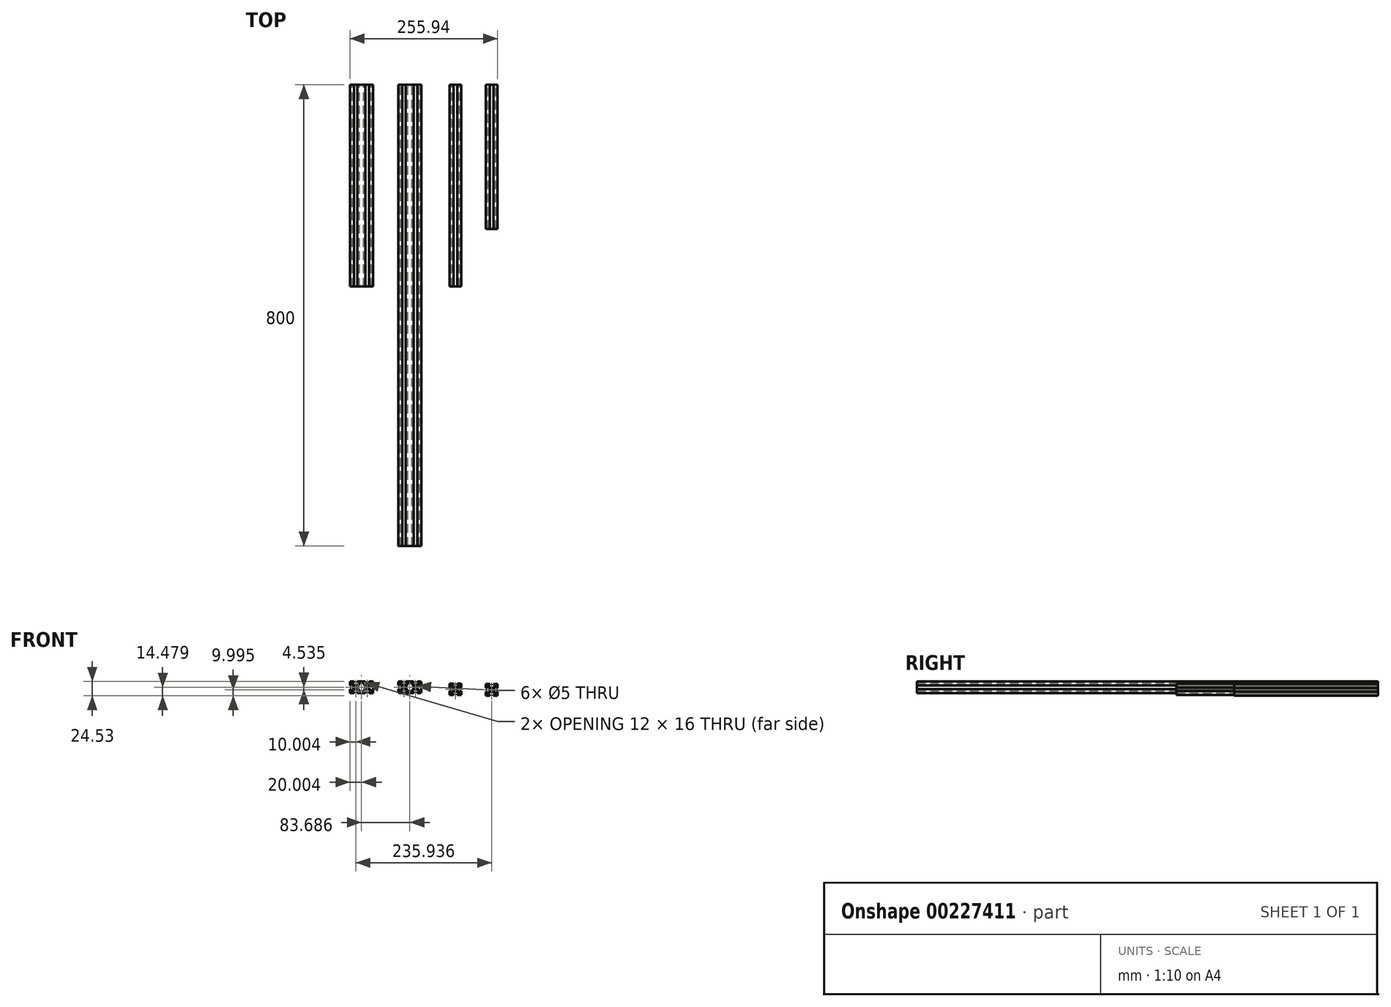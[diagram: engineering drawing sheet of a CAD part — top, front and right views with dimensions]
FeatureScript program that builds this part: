
annotation { "Feature Type Name" : "Feature", "Feature Type Description" : "" }
export const myFeature = defineFeature(function(context is Context, id is Id, definition is map)
    precondition{}
    {
        {
            var Q0;
            Q0=qCreatedBy(makeId("Front.planeOp"),FACE);
            var sketch = newSketch(context, id + "F0", { "sketchPlane" : qUnion([Q0])});
            skLineSegment(sketch, "E0.bottom", {"start": v(-20, 10) * mm, "end": v(-13, 10) * mm});
            skLineSegment(sketch, "E0.top", {"start": v(-20, -10) * mm, "end": v(-13, -10) * mm});
            skLineSegment(sketch, "E0.left", {"start": v(-20, 10) * mm, "end": v(-20, 3) * mm});
            skPoint(sketch, "E1.endSnap0", {"position": v(0, -10) * mm});
            skLineSegment(sketch, "E2", {"start": v(-26.6, 0) * mm, "end": v(32.73, 0) * mm, "construction": true});
            skCircle(sketch, "E3", {"center": v(10, 0) * mm, "radius": 2.5 * mm});
            skCircle(sketch, "E4", {"center": v(-10, 0) * mm, "radius": 2.5 * mm});
            skLineSegment(sketch, "E5", {"start": v(4.5, 8) * mm, "end": v(7, 8) * mm});
            skLineSegment(sketch, "E6", {"start": v(15.5, 8) * mm, "end": v(15.5, 6.5) * mm});
            skLineSegment(sketch, "E7", {"start": v(15.5, 6.5) * mm, "end": v(13, 4) * mm});
            skLineSegment(sketch, "E8", {"start": v(13, 4) * mm, "end": v(7, 4) * mm});
            skLineSegment(sketch, "E9", {"start": v(7, 4) * mm, "end": v(4.5, 6.5) * mm});
            skLineSegment(sketch, "E10", {"start": v(4.5, 6.5) * mm, "end": v(4.5, 8) * mm});
            skLineSegment(sketch, "E11", {"start": v(0, 29.93) * mm, "end": v(0, -23.02) * mm, "construction": true});
            skLineSegment(sketch, "E12", {"start": v(7, 8) * mm, "end": v(7, 10) * mm});
            skLineSegment(sketch, "E13", {"start": v(13, 8) * mm, "end": v(13, 10) * mm});
            skLineSegment(sketch, "E14.trimOffspring", {"start": v(13, 8) * mm, "end": v(15.5, 8) * mm});
            skLineSegment(sketch, "E15.trimOffspring", {"start": v(13, 10) * mm, "end": v(20, 10) * mm});
            skLineSegment(sketch, "E16.1.3", {"start": v(6, -3) * mm, "end": v(3.5, -5.5) * mm});
            skLineSegment(sketch, "E16.1.4", {"start": v(6, 3) * mm, "end": v(6, -3) * mm});
            skLineSegment(sketch, "E16.1.5", {"start": v(3.5, 5.5) * mm, "end": v(6, 3) * mm});
            skLineSegment(sketch, "E16.2.0", {"start": v(13, -8) * mm, "end": v(13, -10) * mm});
            skLineSegment(sketch, "E16.2.1", {"start": v(15.5, -8) * mm, "end": v(13, -8) * mm});
            skLineSegment(sketch, "E16.2.2", {"start": v(15.5, -6.5) * mm, "end": v(15.5, -8) * mm});
            skLineSegment(sketch, "E16.2.3", {"start": v(13, -4) * mm, "end": v(15.5, -6.5) * mm});
            skLineSegment(sketch, "E16.2.4", {"start": v(7, -4) * mm, "end": v(13, -4) * mm});
            skLineSegment(sketch, "E16.2.5", {"start": v(4.5, -6.5) * mm, "end": v(7, -4) * mm});
            skLineSegment(sketch, "E16.2.6", {"start": v(7, -8) * mm, "end": v(7, -10) * mm});
            skLineSegment(sketch, "E16.2.7", {"start": v(7, -8) * mm, "end": v(4.5, -8) * mm});
            skLineSegment(sketch, "E16.2.8", {"start": v(4.5, -8) * mm, "end": v(4.5, -6.5) * mm});
            skLineSegment(sketch, "E16.3.0", {"start": v(18, 3) * mm, "end": v(20, 3) * mm});
            skLineSegment(sketch, "E16.3.1", {"start": v(18, 5.5) * mm, "end": v(18, 3) * mm});
            skLineSegment(sketch, "E16.3.2", {"start": v(16.5, 5.5) * mm, "end": v(18, 5.5) * mm});
            skLineSegment(sketch, "E16.3.3", {"start": v(14, 3) * mm, "end": v(16.5, 5.5) * mm});
            skLineSegment(sketch, "E16.3.4", {"start": v(14, -3) * mm, "end": v(14, 3) * mm});
            skLineSegment(sketch, "E16.3.5", {"start": v(16.5, -5.5) * mm, "end": v(14, -3) * mm});
            skLineSegment(sketch, "E16.3.6", {"start": v(18, -3) * mm, "end": v(20, -3) * mm});
            skLineSegment(sketch, "E16.3.7", {"start": v(18, -3) * mm, "end": v(18, -5.5) * mm});
            skLineSegment(sketch, "E16.3.8", {"start": v(18, -5.5) * mm, "end": v(16.5, -5.5) * mm});
            skLineSegment(sketch, "E17.MirrorCS", {"start": v(-4.5, -8) * mm, "end": v(-4.5, -6.5) * mm});
            skLineSegment(sketch, "E18.MirrorCS", {"start": v(-4.5, -6.5) * mm, "end": v(-7, -4) * mm});
            skLineSegment(sketch, "E19.MirrorCS", {"start": v(-7, -4) * mm, "end": v(-13, -4) * mm});
            skLineSegment(sketch, "E20.MirrorCS", {"start": v(-7, -8) * mm, "end": v(-4.5, -8) * mm});
            skLineSegment(sketch, "E21.MirrorCS", {"start": v(-7, -8) * mm, "end": v(-7, -10) * mm});
            skLineSegment(sketch, "E22.MirrorCS", {"start": v(-13, -8) * mm, "end": v(-13, -10) * mm});
            skLineSegment(sketch, "E23.MirrorCS", {"start": v(-15.5, -8) * mm, "end": v(-13, -8) * mm});
            skLineSegment(sketch, "E24.MirrorCS", {"start": v(-15.5, -6.5) * mm, "end": v(-15.5, -8) * mm});
            skLineSegment(sketch, "E25.MirrorCS", {"start": v(-13, -4) * mm, "end": v(-15.5, -6.5) * mm});
            skLineSegment(sketch, "E26.MirrorCS", {"start": v(-14, -3) * mm, "end": v(-14, 3) * mm});
            skLineSegment(sketch, "E27.MirrorCS", {"start": v(-16.5, -5.5) * mm, "end": v(-14, -3) * mm});
            skLineSegment(sketch, "E28.MirrorCS", {"start": v(-18, -5.5) * mm, "end": v(-16.5, -5.5) * mm});
            skLineSegment(sketch, "E29.MirrorCS", {"start": v(-18, -3) * mm, "end": v(-18, -5.5) * mm});
            skLineSegment(sketch, "E30.MirrorCS", {"start": v(-18, -3) * mm, "end": v(-20, -3) * mm});
            skLineSegment(sketch, "E31.MirrorCS", {"start": v(-18, 3) * mm, "end": v(-20, 3) * mm});
            skLineSegment(sketch, "E32.MirrorCS", {"start": v(-16.5, 5.5) * mm, "end": v(-18, 5.5) * mm});
            skLineSegment(sketch, "E33.MirrorCS", {"start": v(-14, 3) * mm, "end": v(-16.5, 5.5) * mm});
            skLineSegment(sketch, "E34.MirrorCS", {"start": v(-18, 5.5) * mm, "end": v(-18, 3) * mm});
            skLineSegment(sketch, "E35.MirrorCS", {"start": v(-7, 8) * mm, "end": v(-7, 10) * mm});
            skLineSegment(sketch, "E36.MirrorCS", {"start": v(-4.5, 8) * mm, "end": v(-7, 8) * mm});
            skLineSegment(sketch, "E37.MirrorCS", {"start": v(-4.5, 6.5) * mm, "end": v(-4.5, 8) * mm});
            skLineSegment(sketch, "E38.MirrorCS", {"start": v(-7, 4) * mm, "end": v(-4.5, 6.5) * mm});
            skLineSegment(sketch, "E39.MirrorCS", {"start": v(-13, 4) * mm, "end": v(-7, 4) * mm});
            skLineSegment(sketch, "E40.MirrorCS", {"start": v(-15.5, 6.5) * mm, "end": v(-13, 4) * mm});
            skLineSegment(sketch, "E41.MirrorCS", {"start": v(-15.5, 8) * mm, "end": v(-15.5, 6.5) * mm});
            skLineSegment(sketch, "E42.MirrorCS", {"start": v(-13, 8) * mm, "end": v(-15.5, 8) * mm});
            skLineSegment(sketch, "E43.MirrorCS", {"start": v(-13, 8) * mm, "end": v(-13, 10) * mm});
            skLineSegment(sketch, "E44.MirrorCS", {"start": v(-3.5, 5.5) * mm, "end": v(-6, 3) * mm});
            skLineSegment(sketch, "E45.MirrorCS", {"start": v(-6, 3) * mm, "end": v(-6, -3) * mm});
            skLineSegment(sketch, "E46.MirrorCS", {"start": v(-6, -3) * mm, "end": v(-3.5, -5.5) * mm});
            skLineSegment(sketch, "E47", {"start": v(-3.5, 5.5) * mm, "end": v(-3.5, 8) * mm});
            skLineSegment(sketch, "E48", {"start": v(3.5, 5.5) * mm, "end": v(3.5, 8) * mm});
            skLineSegment(sketch, "E49", {"start": v(3.5, 8) * mm, "end": v(-3.5, 8) * mm});
            skLineSegment(sketch, "E50.trimOffspring", {"start": v(-20, -3) * mm, "end": v(-20, -10) * mm});
            skLineSegment(sketch, "E51.trimOffspring", {"start": v(-7, 10) * mm, "end": v(7, 10) * mm});
            skLineSegment(sketch, "E52.trimOffspring", {"start": v(20, -3) * mm, "end": v(20, -10) * mm});
            skLineSegment(sketch, "E53.trimOffspring", {"start": v(13, -10) * mm, "end": v(20, -10) * mm});
            skLineSegment(sketch, "E54.trimOffspring", {"start": v(-7, -10) * mm, "end": v(7, -10) * mm});
            skLineSegment(sketch, "E55.MirrorCS", {"start": v(-3.5, -5.5) * mm, "end": v(-3.5, -8) * mm});
            skLineSegment(sketch, "E56.MirrorCS", {"start": v(3.5, -8) * mm, "end": v(-3.5, -8) * mm});
            skLineSegment(sketch, "E57.MirrorCS", {"start": v(3.5, -5.5) * mm, "end": v(3.5, -8) * mm});
            skLineSegment(sketch, "E58", {"start": v(20, 10) * mm, "end": v(20, 3) * mm});
            skSolve(sketch);
        }
        {
            var Q0;
            Q0 = qSketchRegion(id + "F0", true);
            extrude(context, id + "F1", {"entities" : qUnion([Q0]), "depth" : 800 * mm});
        }
        {
            var Q0;
            Q0=makeQuery(id+"F1.opExtrude","SWEPT_EDGE",EDGE,{"disambiguationData":[OSD([sQuery(id+"F0.wireOp",EDGE,"E15.trimOffspring"),sQuery(id+"F0.wireOp",EDGE,"E58")])]});
            var Q1;
            Q1=makeQuery(id+"F1.opExtrude","SWEPT_EDGE",EDGE,{"disambiguationData":[OSD([sQuery(id+"F0.wireOp",EDGE,"E0.bottom"),sQuery(id+"F0.wireOp",EDGE,"E0.left")])]});
            var Q2;
            Q2=makeQuery(id+"F1.opExtrude","SWEPT_EDGE",EDGE,{"disambiguationData":[OSD([sQuery(id+"F0.wireOp",EDGE,"E0.top"),sQuery(id+"F0.wireOp",EDGE,"E50.trimOffspring")])]});
            var Q3;
            Q3=makeQuery(id+"F1.opExtrude","SWEPT_EDGE",EDGE,{"disambiguationData":[OSD([sQuery(id+"F0.wireOp",EDGE,"E52.trimOffspring"),sQuery(id+"F0.wireOp",EDGE,"E53.trimOffspring")])]});
            fillet(context, id + "F2", {"entities" : qUnion([Q0, Q1, Q2, Q3]), "radius" : 2 * mm, "tangentPropagation" : true, "allowEdgeOverflow" : false});
        }
        {
            var Q0;
            Q0=qCreatedBy(makeId("Front.planeOp"),FACE);
            var sketch = newSketch(context, id + "F3", { "sketchPlane" : qUnion([Q0])});
            skLineSegment(sketch, "E59.bottom", {"start": v(-103.69, 9.95) * mm, "end": v(-96.69, 9.95) * mm});
            skLineSegment(sketch, "E59.top", {"start": v(-103.69, -10.05) * mm, "end": v(-96.69, -10.05) * mm});
            skLineSegment(sketch, "E59.left", {"start": v(-103.69, 9.95) * mm, "end": v(-103.69, 2.95) * mm});
            skPoint(sketch, "E60.endSnap0", {"position": v(-83.69, -10.05) * mm});
            skLineSegment(sketch, "E61", {"start": v(-110.28, -0.05) * mm, "end": v(-50.95, -0.05) * mm, "construction": true});
            skCircle(sketch, "E62", {"center": v(-73.69, -0.05) * mm, "radius": 2.5 * mm});
            skCircle(sketch, "E63", {"center": v(-93.69, -0.05) * mm, "radius": 2.5 * mm});
            skLineSegment(sketch, "E64", {"start": v(-79.19, 7.95) * mm, "end": v(-76.69, 7.95) * mm});
            skLineSegment(sketch, "E65", {"start": v(-68.19, 7.95) * mm, "end": v(-68.19, 6.45) * mm});
            skLineSegment(sketch, "E66", {"start": v(-68.19, 6.45) * mm, "end": v(-70.69, 3.95) * mm});
            skLineSegment(sketch, "E67", {"start": v(-70.69, 3.95) * mm, "end": v(-76.69, 3.95) * mm});
            skLineSegment(sketch, "E68", {"start": v(-76.69, 3.95) * mm, "end": v(-79.19, 6.45) * mm});
            skLineSegment(sketch, "E69", {"start": v(-79.19, 6.45) * mm, "end": v(-79.19, 7.95) * mm});
            skLineSegment(sketch, "E70", {"start": v(-83.69, 29.88) * mm, "end": v(-83.69, -23.07) * mm, "construction": true});
            skLineSegment(sketch, "E71", {"start": v(-76.69, 7.95) * mm, "end": v(-76.69, 9.95) * mm});
            skLineSegment(sketch, "E72", {"start": v(-70.69, 7.95) * mm, "end": v(-70.69, 9.95) * mm});
            skLineSegment(sketch, "E73.trimOffspring", {"start": v(-70.69, 7.95) * mm, "end": v(-68.19, 7.95) * mm});
            skLineSegment(sketch, "E74.trimOffspring", {"start": v(-70.69, 9.95) * mm, "end": v(-63.69, 9.95) * mm});
            skLineSegment(sketch, "E75.1.3", {"start": v(-77.69, -3.05) * mm, "end": v(-80.19, -5.55) * mm});
            skLineSegment(sketch, "E75.1.4", {"start": v(-77.69, 2.95) * mm, "end": v(-77.69, -3.05) * mm});
            skLineSegment(sketch, "E75.1.5", {"start": v(-80.19, 5.45) * mm, "end": v(-77.69, 2.95) * mm});
            skLineSegment(sketch, "E75.2.0", {"start": v(-70.69, -8.05) * mm, "end": v(-70.69, -10.05) * mm});
            skLineSegment(sketch, "E75.2.1", {"start": v(-68.19, -8.05) * mm, "end": v(-70.69, -8.05) * mm});
            skLineSegment(sketch, "E75.2.2", {"start": v(-68.19, -6.55) * mm, "end": v(-68.19, -8.05) * mm});
            skLineSegment(sketch, "E75.2.3", {"start": v(-70.69, -4.05) * mm, "end": v(-68.19, -6.55) * mm});
            skLineSegment(sketch, "E75.2.4", {"start": v(-76.69, -4.05) * mm, "end": v(-70.69, -4.05) * mm});
            skLineSegment(sketch, "E75.2.5", {"start": v(-79.19, -6.55) * mm, "end": v(-76.69, -4.05) * mm});
            skLineSegment(sketch, "E75.2.6", {"start": v(-76.69, -8.05) * mm, "end": v(-76.69, -10.05) * mm});
            skLineSegment(sketch, "E75.2.7", {"start": v(-76.69, -8.05) * mm, "end": v(-79.19, -8.05) * mm});
            skLineSegment(sketch, "E75.2.8", {"start": v(-79.19, -8.05) * mm, "end": v(-79.19, -6.55) * mm});
            skLineSegment(sketch, "E75.3.0", {"start": v(-65.69, 2.95) * mm, "end": v(-63.69, 2.95) * mm});
            skLineSegment(sketch, "E75.3.1", {"start": v(-65.69, 5.45) * mm, "end": v(-65.69, 2.95) * mm});
            skLineSegment(sketch, "E75.3.2", {"start": v(-67.19, 5.45) * mm, "end": v(-65.69, 5.45) * mm});
            skLineSegment(sketch, "E75.3.3", {"start": v(-69.69, 2.95) * mm, "end": v(-67.19, 5.45) * mm});
            skLineSegment(sketch, "E75.3.4", {"start": v(-69.69, -3.05) * mm, "end": v(-69.69, 2.95) * mm});
            skLineSegment(sketch, "E75.3.5", {"start": v(-67.19, -5.55) * mm, "end": v(-69.69, -3.05) * mm});
            skLineSegment(sketch, "E75.3.6", {"start": v(-65.69, -3.05) * mm, "end": v(-63.69, -3.05) * mm});
            skLineSegment(sketch, "E75.3.7", {"start": v(-65.69, -3.05) * mm, "end": v(-65.69, -5.55) * mm});
            skLineSegment(sketch, "E75.3.8", {"start": v(-65.69, -5.55) * mm, "end": v(-67.19, -5.55) * mm});
            skLineSegment(sketch, "E76.MirrorCS", {"start": v(-88.19, -8.05) * mm, "end": v(-88.19, -6.55) * mm});
            skLineSegment(sketch, "E77.MirrorCS", {"start": v(-88.19, -6.55) * mm, "end": v(-90.69, -4.05) * mm});
            skLineSegment(sketch, "E78.MirrorCS", {"start": v(-90.69, -4.05) * mm, "end": v(-96.69, -4.05) * mm});
            skLineSegment(sketch, "E79.MirrorCS", {"start": v(-90.69, -8.05) * mm, "end": v(-88.19, -8.05) * mm});
            skLineSegment(sketch, "E80.MirrorCS", {"start": v(-90.69, -8.05) * mm, "end": v(-90.69, -10.05) * mm});
            skLineSegment(sketch, "E81.MirrorCS", {"start": v(-96.69, -8.05) * mm, "end": v(-96.69, -10.05) * mm});
            skLineSegment(sketch, "E82.MirrorCS", {"start": v(-99.19, -8.05) * mm, "end": v(-96.69, -8.05) * mm});
            skLineSegment(sketch, "E83.MirrorCS", {"start": v(-99.19, -6.55) * mm, "end": v(-99.19, -8.05) * mm});
            skLineSegment(sketch, "E84.MirrorCS", {"start": v(-96.69, -4.05) * mm, "end": v(-99.19, -6.55) * mm});
            skLineSegment(sketch, "E85.MirrorCS", {"start": v(-97.69, -3.05) * mm, "end": v(-97.69, 2.95) * mm});
            skLineSegment(sketch, "E86.MirrorCS", {"start": v(-100.19, -5.55) * mm, "end": v(-97.69, -3.05) * mm});
            skLineSegment(sketch, "E87.MirrorCS", {"start": v(-101.69, -5.55) * mm, "end": v(-100.19, -5.55) * mm});
            skLineSegment(sketch, "E88.MirrorCS", {"start": v(-101.69, -3.05) * mm, "end": v(-101.69, -5.55) * mm});
            skLineSegment(sketch, "E89.MirrorCS", {"start": v(-101.69, -3.05) * mm, "end": v(-103.69, -3.05) * mm});
            skLineSegment(sketch, "E90.MirrorCS", {"start": v(-101.69, 2.95) * mm, "end": v(-103.69, 2.95) * mm});
            skLineSegment(sketch, "E91.MirrorCS", {"start": v(-100.19, 5.45) * mm, "end": v(-101.69, 5.45) * mm});
            skLineSegment(sketch, "E92.MirrorCS", {"start": v(-97.69, 2.95) * mm, "end": v(-100.19, 5.45) * mm});
            skLineSegment(sketch, "E93.MirrorCS", {"start": v(-101.69, 5.45) * mm, "end": v(-101.69, 2.95) * mm});
            skLineSegment(sketch, "E94.MirrorCS", {"start": v(-90.69, 7.95) * mm, "end": v(-90.69, 9.95) * mm});
            skLineSegment(sketch, "E95.MirrorCS", {"start": v(-88.19, 7.95) * mm, "end": v(-90.69, 7.95) * mm});
            skLineSegment(sketch, "E96.MirrorCS", {"start": v(-88.19, 6.45) * mm, "end": v(-88.19, 7.95) * mm});
            skLineSegment(sketch, "E97.MirrorCS", {"start": v(-90.69, 3.95) * mm, "end": v(-88.19, 6.45) * mm});
            skLineSegment(sketch, "E98.MirrorCS", {"start": v(-96.69, 3.95) * mm, "end": v(-90.69, 3.95) * mm});
            skLineSegment(sketch, "E99.MirrorCS", {"start": v(-99.19, 6.45) * mm, "end": v(-96.69, 3.95) * mm});
            skLineSegment(sketch, "E100.MirrorCS", {"start": v(-99.19, 7.95) * mm, "end": v(-99.19, 6.45) * mm});
            skLineSegment(sketch, "E101.MirrorCS", {"start": v(-96.69, 7.95) * mm, "end": v(-99.19, 7.95) * mm});
            skLineSegment(sketch, "E102.MirrorCS", {"start": v(-96.69, 7.95) * mm, "end": v(-96.69, 9.95) * mm});
            skLineSegment(sketch, "E103.MirrorCS", {"start": v(-87.19, 5.45) * mm, "end": v(-89.69, 2.95) * mm});
            skLineSegment(sketch, "E104.MirrorCS", {"start": v(-89.69, 2.95) * mm, "end": v(-89.69, -3.05) * mm});
            skLineSegment(sketch, "E105.MirrorCS", {"start": v(-89.69, -3.05) * mm, "end": v(-87.19, -5.55) * mm});
            skLineSegment(sketch, "E106", {"start": v(-87.19, 5.45) * mm, "end": v(-87.19, 7.95) * mm});
            skLineSegment(sketch, "E107", {"start": v(-80.19, 5.45) * mm, "end": v(-80.19, 7.95) * mm});
            skLineSegment(sketch, "E108", {"start": v(-80.19, 7.95) * mm, "end": v(-87.19, 7.95) * mm});
            skLineSegment(sketch, "E109.trimOffspring", {"start": v(-103.69, -3.05) * mm, "end": v(-103.69, -10.05) * mm});
            skLineSegment(sketch, "E110.trimOffspring", {"start": v(-90.69, 9.95) * mm, "end": v(-76.69, 9.95) * mm});
            skLineSegment(sketch, "E111.trimOffspring", {"start": v(-63.69, -3.05) * mm, "end": v(-63.69, -10.05) * mm});
            skLineSegment(sketch, "E112.trimOffspring", {"start": v(-70.69, -10.05) * mm, "end": v(-63.69, -10.05) * mm});
            skLineSegment(sketch, "E113.trimOffspring", {"start": v(-90.69, -10.05) * mm, "end": v(-76.69, -10.05) * mm});
            skLineSegment(sketch, "E114.MirrorCS", {"start": v(-87.19, -5.55) * mm, "end": v(-87.19, -8.05) * mm});
            skLineSegment(sketch, "E115.MirrorCS", {"start": v(-80.19, -8.05) * mm, "end": v(-87.19, -8.05) * mm});
            skLineSegment(sketch, "E116.MirrorCS", {"start": v(-80.19, -5.55) * mm, "end": v(-80.19, -8.05) * mm});
            skLineSegment(sketch, "E117", {"start": v(-63.69, 9.95) * mm, "end": v(-63.69, 2.95) * mm});
            skSolve(sketch);
        }
        {
            var Q0;
            Q0 = qSketchRegion(id + "F3", true);
            extrude(context, id + "F4", {"entities" : qUnion([Q0]), "depth" : 350 * mm});
        }
        {
            var Q0;
            Q0=qCreatedBy(makeId("Front.planeOp"),FACE);
            var sketch = newSketch(context, id + "F5", { "sketchPlane" : qUnion([Q0])});
            skPoint(sketch, "E118.endSnap0", {"position": v(69.36, -13.62) * mm});
            skLineSegment(sketch, "E119", {"start": v(42.77, -3.62) * mm, "end": v(102.1, -3.62) * mm, "construction": true});
            skCircle(sketch, "E120", {"center": v(79.36, -3.62) * mm, "radius": 2.5 * mm});
            skLineSegment(sketch, "E121", {"start": v(84.86, 4.37) * mm, "end": v(84.86, 2.87) * mm});
            skLineSegment(sketch, "E122", {"start": v(84.86, 2.87) * mm, "end": v(82.36, 0.37) * mm});
            skLineSegment(sketch, "E123", {"start": v(82.36, 0.37) * mm, "end": v(76.36, 0.37) * mm});
            skLineSegment(sketch, "E124", {"start": v(76.36, 0.37) * mm, "end": v(73.86, 2.87) * mm});
            skLineSegment(sketch, "E125", {"start": v(73.86, 2.87) * mm, "end": v(73.86, 4.37) * mm});
            skLineSegment(sketch, "E126", {"start": v(76.36, 4.37) * mm, "end": v(76.36, 6.38) * mm});
            skLineSegment(sketch, "E127", {"start": v(82.36, 4.37) * mm, "end": v(82.36, 6.38) * mm});
            skLineSegment(sketch, "E128.trimOffspring", {"start": v(82.36, 4.37) * mm, "end": v(84.86, 4.37) * mm});
            skLineSegment(sketch, "E129.trimOffspring", {"start": v(82.36, 6.38) * mm, "end": v(89.36, 6.38) * mm});
            skLineSegment(sketch, "E130.1.3", {"start": v(75.36, -6.62) * mm, "end": v(72.86, -9.12) * mm});
            skLineSegment(sketch, "E130.1.4", {"start": v(75.36, -0.62) * mm, "end": v(75.36, -6.62) * mm});
            skLineSegment(sketch, "E130.1.5", {"start": v(72.86, 1.88) * mm, "end": v(75.36, -0.62) * mm});
            skLineSegment(sketch, "E130.2.0", {"start": v(82.36, -11.62) * mm, "end": v(82.36, -13.62) * mm});
            skLineSegment(sketch, "E130.2.1", {"start": v(84.86, -11.62) * mm, "end": v(82.36, -11.62) * mm});
            skLineSegment(sketch, "E130.2.2", {"start": v(84.86, -10.12) * mm, "end": v(84.86, -11.62) * mm});
            skLineSegment(sketch, "E130.2.3", {"start": v(82.36, -7.62) * mm, "end": v(84.86, -10.12) * mm});
            skLineSegment(sketch, "E130.2.4", {"start": v(76.36, -7.62) * mm, "end": v(82.36, -7.62) * mm});
            skLineSegment(sketch, "E130.2.5", {"start": v(73.86, -10.12) * mm, "end": v(76.36, -7.62) * mm});
            skLineSegment(sketch, "E130.2.6", {"start": v(76.36, -11.62) * mm, "end": v(76.36, -13.62) * mm});
            skLineSegment(sketch, "E130.2.7", {"start": v(76.36, -11.62) * mm, "end": v(73.86, -11.62) * mm});
            skLineSegment(sketch, "E130.2.8", {"start": v(73.86, -11.62) * mm, "end": v(73.86, -10.12) * mm});
            skLineSegment(sketch, "E130.3.0", {"start": v(87.36, -0.62) * mm, "end": v(89.36, -0.62) * mm});
            skLineSegment(sketch, "E130.3.1", {"start": v(87.36, 1.88) * mm, "end": v(87.36, -0.62) * mm});
            skLineSegment(sketch, "E130.3.2", {"start": v(85.86, 1.88) * mm, "end": v(87.36, 1.88) * mm});
            skLineSegment(sketch, "E130.3.3", {"start": v(83.36, -0.62) * mm, "end": v(85.86, 1.88) * mm});
            skLineSegment(sketch, "E130.3.4", {"start": v(83.36, -6.62) * mm, "end": v(83.36, -0.62) * mm});
            skLineSegment(sketch, "E130.3.5", {"start": v(85.86, -9.12) * mm, "end": v(83.36, -6.62) * mm});
            skLineSegment(sketch, "E130.3.6", {"start": v(87.36, -6.62) * mm, "end": v(89.36, -6.62) * mm});
            skLineSegment(sketch, "E130.3.7", {"start": v(87.36, -6.62) * mm, "end": v(87.36, -9.12) * mm});
            skLineSegment(sketch, "E130.3.8", {"start": v(87.36, -9.12) * mm, "end": v(85.86, -9.12) * mm});
            skLineSegment(sketch, "E131.trimOffspring", {"start": v(69.36, 6.38) * mm, "end": v(76.36, 6.38) * mm});
            skLineSegment(sketch, "E132.trimOffspring", {"start": v(89.36, -6.62) * mm, "end": v(89.36, -13.62) * mm});
            skLineSegment(sketch, "E133.trimOffspring", {"start": v(82.36, -13.62) * mm, "end": v(89.36, -13.62) * mm});
            skLineSegment(sketch, "E134.trimOffspring", {"start": v(69.36, -13.62) * mm, "end": v(76.36, -13.62) * mm});
            skLineSegment(sketch, "E135", {"start": v(89.36, 6.38) * mm, "end": v(89.36, -0.62) * mm});
            skLineSegment(sketch, "E136", {"start": v(79.36, -3.62) * mm, "end": v(79.36, -16.55) * mm, "construction": true});
            skLineSegment(sketch, "E137.MirrorCS", {"start": v(69.36, -6.62) * mm, "end": v(69.36, -13.62) * mm});
            skLineSegment(sketch, "E138.MirrorCS", {"start": v(71.36, -9.12) * mm, "end": v(72.86, -9.12) * mm});
            skLineSegment(sketch, "E139.MirrorCS", {"start": v(71.36, -6.62) * mm, "end": v(71.36, -9.12) * mm});
            skLineSegment(sketch, "E140.MirrorCS", {"start": v(76.36, 4.37) * mm, "end": v(73.86, 4.37) * mm});
            skLineSegment(sketch, "E141.MirrorCS", {"start": v(69.36, 6.38) * mm, "end": v(69.36, -0.62) * mm});
            skLineSegment(sketch, "E142.MirrorCS", {"start": v(71.36, 1.88) * mm, "end": v(71.36, -0.62) * mm});
            skLineSegment(sketch, "E143.MirrorCS", {"start": v(71.36, -0.62) * mm, "end": v(69.36, -0.62) * mm});
            skLineSegment(sketch, "E144.MirrorCS", {"start": v(72.86, 1.88) * mm, "end": v(71.36, 1.88) * mm});
            skLineSegment(sketch, "E145", {"start": v(69.36, -6.62) * mm, "end": v(71.36, -6.62) * mm});
            skSolve(sketch);
        }
        {
            var Q0;
            Q0 = qSketchRegion(id + "F5", true);
            extrude(context, id + "F6", {"entities" : qUnion([Q0]), "depth" : 350 * mm});
        }
        {
            var Q0;
            Q0=qCreatedBy(makeId("Front.planeOp"),FACE);
            var sketch = newSketch(context, id + "F7", { "sketchPlane" : qUnion([Q0])});
            skPoint(sketch, "E146.endSnap0", {"position": v(132.25, -14.53) * mm});
            skCircle(sketch, "E147", {"center": v(142.25, -4.53) * mm, "radius": 2.5 * mm});
            skLineSegment(sketch, "E148", {"start": v(147.75, 3.46) * mm, "end": v(147.75, 1.96) * mm});
            skLineSegment(sketch, "E149", {"start": v(147.75, 1.96) * mm, "end": v(145.25, -0.54) * mm});
            skLineSegment(sketch, "E150", {"start": v(145.25, -0.54) * mm, "end": v(139.25, -0.54) * mm});
            skLineSegment(sketch, "E151", {"start": v(139.25, -0.54) * mm, "end": v(136.75, 1.96) * mm});
            skLineSegment(sketch, "E152", {"start": v(136.75, 1.96) * mm, "end": v(136.75, 3.46) * mm});
            skLineSegment(sketch, "E153", {"start": v(139.25, 3.46) * mm, "end": v(139.25, 5.47) * mm});
            skLineSegment(sketch, "E154", {"start": v(145.25, 3.46) * mm, "end": v(145.25, 5.47) * mm});
            skLineSegment(sketch, "E155.trimOffspring", {"start": v(145.25, 3.46) * mm, "end": v(147.75, 3.46) * mm});
            skLineSegment(sketch, "E156.trimOffspring", {"start": v(145.25, 5.47) * mm, "end": v(152.25, 5.47) * mm});
            skLineSegment(sketch, "E157.1.3", {"start": v(138.25, -7.53) * mm, "end": v(135.75, -10.03) * mm});
            skLineSegment(sketch, "E157.1.4", {"start": v(138.25, -1.53) * mm, "end": v(138.25, -7.53) * mm});
            skLineSegment(sketch, "E157.1.5", {"start": v(135.75, 0.97) * mm, "end": v(138.25, -1.53) * mm});
            skLineSegment(sketch, "E157.2.0", {"start": v(145.25, -12.53) * mm, "end": v(145.25, -14.53) * mm});
            skLineSegment(sketch, "E157.2.1", {"start": v(147.75, -12.53) * mm, "end": v(145.25, -12.53) * mm});
            skLineSegment(sketch, "E157.2.2", {"start": v(147.75, -11.03) * mm, "end": v(147.75, -12.53) * mm});
            skLineSegment(sketch, "E157.2.3", {"start": v(145.25, -8.53) * mm, "end": v(147.75, -11.03) * mm});
            skLineSegment(sketch, "E157.2.4", {"start": v(139.25, -8.53) * mm, "end": v(145.25, -8.53) * mm});
            skLineSegment(sketch, "E157.2.5", {"start": v(136.75, -11.03) * mm, "end": v(139.25, -8.53) * mm});
            skLineSegment(sketch, "E157.2.6", {"start": v(139.25, -12.53) * mm, "end": v(139.25, -14.53) * mm});
            skLineSegment(sketch, "E157.2.7", {"start": v(139.25, -12.53) * mm, "end": v(136.75, -12.53) * mm});
            skLineSegment(sketch, "E157.2.8", {"start": v(136.75, -12.53) * mm, "end": v(136.75, -11.03) * mm});
            skLineSegment(sketch, "E157.3.0", {"start": v(150.25, -1.53) * mm, "end": v(152.25, -1.53) * mm});
            skLineSegment(sketch, "E157.3.1", {"start": v(150.25, 0.97) * mm, "end": v(150.25, -1.53) * mm});
            skLineSegment(sketch, "E157.3.2", {"start": v(148.75, 0.97) * mm, "end": v(150.25, 0.97) * mm});
            skLineSegment(sketch, "E157.3.3", {"start": v(146.25, -1.53) * mm, "end": v(148.75, 0.97) * mm});
            skLineSegment(sketch, "E157.3.4", {"start": v(146.25, -7.53) * mm, "end": v(146.25, -1.53) * mm});
            skLineSegment(sketch, "E157.3.5", {"start": v(148.75, -10.03) * mm, "end": v(146.25, -7.53) * mm});
            skLineSegment(sketch, "E157.3.6", {"start": v(150.25, -7.53) * mm, "end": v(152.25, -7.53) * mm});
            skLineSegment(sketch, "E157.3.7", {"start": v(150.25, -7.53) * mm, "end": v(150.25, -10.03) * mm});
            skLineSegment(sketch, "E157.3.8", {"start": v(150.25, -10.03) * mm, "end": v(148.75, -10.03) * mm});
            skLineSegment(sketch, "E158.trimOffspring", {"start": v(132.25, 5.47) * mm, "end": v(139.25, 5.47) * mm});
            skLineSegment(sketch, "E159.trimOffspring", {"start": v(152.25, -7.53) * mm, "end": v(152.25, -14.53) * mm});
            skLineSegment(sketch, "E160.trimOffspring", {"start": v(145.25, -14.53) * mm, "end": v(152.25, -14.53) * mm});
            skLineSegment(sketch, "E161.trimOffspring", {"start": v(132.25, -14.53) * mm, "end": v(139.25, -14.53) * mm});
            skLineSegment(sketch, "E162", {"start": v(152.25, 5.47) * mm, "end": v(152.25, -1.53) * mm});
            skLineSegment(sketch, "E163", {"start": v(142.25, -4.53) * mm, "end": v(142.25, -17.46) * mm, "construction": true});
            skLineSegment(sketch, "E164.MirrorCS", {"start": v(132.25, -7.53) * mm, "end": v(132.25, -14.53) * mm});
            skLineSegment(sketch, "E165.MirrorCS", {"start": v(134.25, -10.03) * mm, "end": v(135.75, -10.03) * mm});
            skLineSegment(sketch, "E166.MirrorCS", {"start": v(134.25, -7.53) * mm, "end": v(134.25, -10.03) * mm});
            skLineSegment(sketch, "E167.MirrorCS", {"start": v(139.25, 3.46) * mm, "end": v(136.75, 3.46) * mm});
            skLineSegment(sketch, "E168.MirrorCS", {"start": v(132.25, 5.47) * mm, "end": v(132.25, -1.53) * mm});
            skLineSegment(sketch, "E169.MirrorCS", {"start": v(134.25, 0.97) * mm, "end": v(134.25, -1.53) * mm});
            skLineSegment(sketch, "E170.MirrorCS", {"start": v(134.25, -1.53) * mm, "end": v(132.25, -1.53) * mm});
            skLineSegment(sketch, "E171.MirrorCS", {"start": v(135.75, 0.97) * mm, "end": v(134.25, 0.97) * mm});
            skLineSegment(sketch, "E172", {"start": v(132.25, -7.53) * mm, "end": v(134.25, -7.53) * mm});
            skSolve(sketch);
        }
        {
            var Q0;
            Q0 = qSketchRegion(id + "F7", true);
            extrude(context, id + "F8", {"entities" : qUnion([Q0]), "depth" : 250 * mm});
        }
    });
